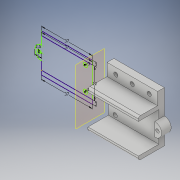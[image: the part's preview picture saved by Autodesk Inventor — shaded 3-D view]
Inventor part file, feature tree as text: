
AUTODESK INVENTOR PART (.ipt)
format: ipt  version: 2019 (Build 230136000, 136)  size: 184,832 bytes
history: native  units: mm
features: extrude x6, sketch x5, other x2, fillet x2, mirror x1, projected_geometry x1
ambient origin geometry x8: Origin, YZ Plane, XZ Plane, XY Plane, X Axis, Y Axis, Z Axis, Center Point
bodies: Body1 (feature_tree)
feature tree (17):
  other  "Bryła1"
  sketch  "Szkic1"
  extrude  "Wyciągnięcie proste1"  Depth=37.0mm
  extrude  "Wyciągnięcie proste2"  Depth=22.0mm
  extrude  "Wyciągnięcie proste3"  Depth=5.0mm
  extrude  "Wyciągnięcie proste4"  Depth=2.5mm
  fillet  "Zaokrąglenie2"  Radius=3.0mm
  fillet  "Zaokrąglenie3"  Radius=3.0mm
  extrude  "Wyciągnięcie proste5"  Depth=37.0mm
  extrude  "Wyciągnięcie proste6"  Depth=3.0mm
  sketch  "Szkic5"
  other  "Płaszczyzna konstrukcyjna1"
  mirror  "Odbij1"
  sketch  "Szkic2"
  sketch  "Szkic3"
  projected_geometry  "Pętla rzutowana1"
  sketch  "Szkic4"
